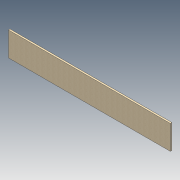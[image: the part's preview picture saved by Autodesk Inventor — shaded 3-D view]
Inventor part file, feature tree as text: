
AUTODESK INVENTOR PART (.ipt)
format: ipt  version: 2012 (Build 160160000, 160)  size: 71,168 bytes
history: native  units: in
note: dims shown in document units (in); Inventor stores cm internally (conversion verified against a paired STEP export)
features: extrude x1, sketch x1
ambient origin geometry x8: Origin, YZ Plane, XZ Plane, XY Plane, X Axis, Y Axis, Z Axis, Center Point
bodies: Solid1 (feature_tree)
feature tree (2):
  extrude  "Extrusion1"  Depth=50.25in
  sketch  "Sketch1"  dims[d0=7.5in d1=50.25in d2=0.5in d3=0.0in]
